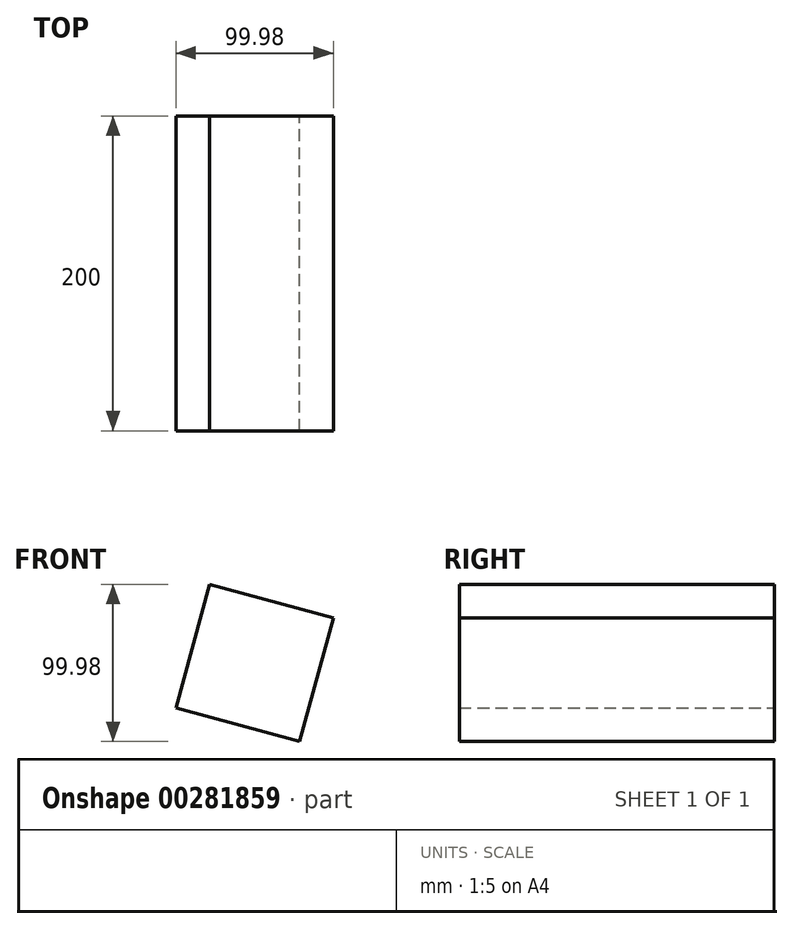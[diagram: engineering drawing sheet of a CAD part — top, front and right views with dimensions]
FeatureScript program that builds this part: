
annotation { "Feature Type Name" : "Feature", "Feature Type Description" : "" }
export const myFeature = defineFeature(function(context is Context, id is Id, definition is map)
    precondition{}
    {
        {
            var Q0;
            Q0=qCreatedBy(makeId("Front.planeOp"),FACE);
            var sketch = newSketch(context, id + "F0", { "sketchPlane" : qUnion([Q0])});
            skCircle(sketch, "E0.cCircle", {"center": v(0, 0) * mm, "radius": 57.57 * mm, "construction": true});
            skLineSegment(sketch, "E0.0", {"start": v(28.56, -49.99) * mm, "end": v(-49.99, -28.56) * mm});
            skLineSegment(sketch, "E0.1", {"start": v(-49.99, -28.56) * mm, "end": v(-28.56, 49.99) * mm});
            skLineSegment(sketch, "E0.2", {"start": v(-28.56, 49.99) * mm, "end": v(49.99, 28.56) * mm});
            skLineSegment(sketch, "E0.3", {"start": v(49.99, 28.56) * mm, "end": v(28.56, -49.99) * mm});
            skSolve(sketch);
        }
        {
            var Q0;
            Q0=makeQuery(id+"F0.imprint","IMPRINT",FACE,{"disambiguationData":[TD([[makeQuery(id+"F0.imprint","IMPRINT",EDGE,{"derivedFrom":sQuery(id+"F0.wireOp",EDGE,"E0.0")}),-1.0]])]});
            extrude(context, id + "F1", {"entities" : qUnion([Q0]), "depth" : 200 * mm});
        }
    });
